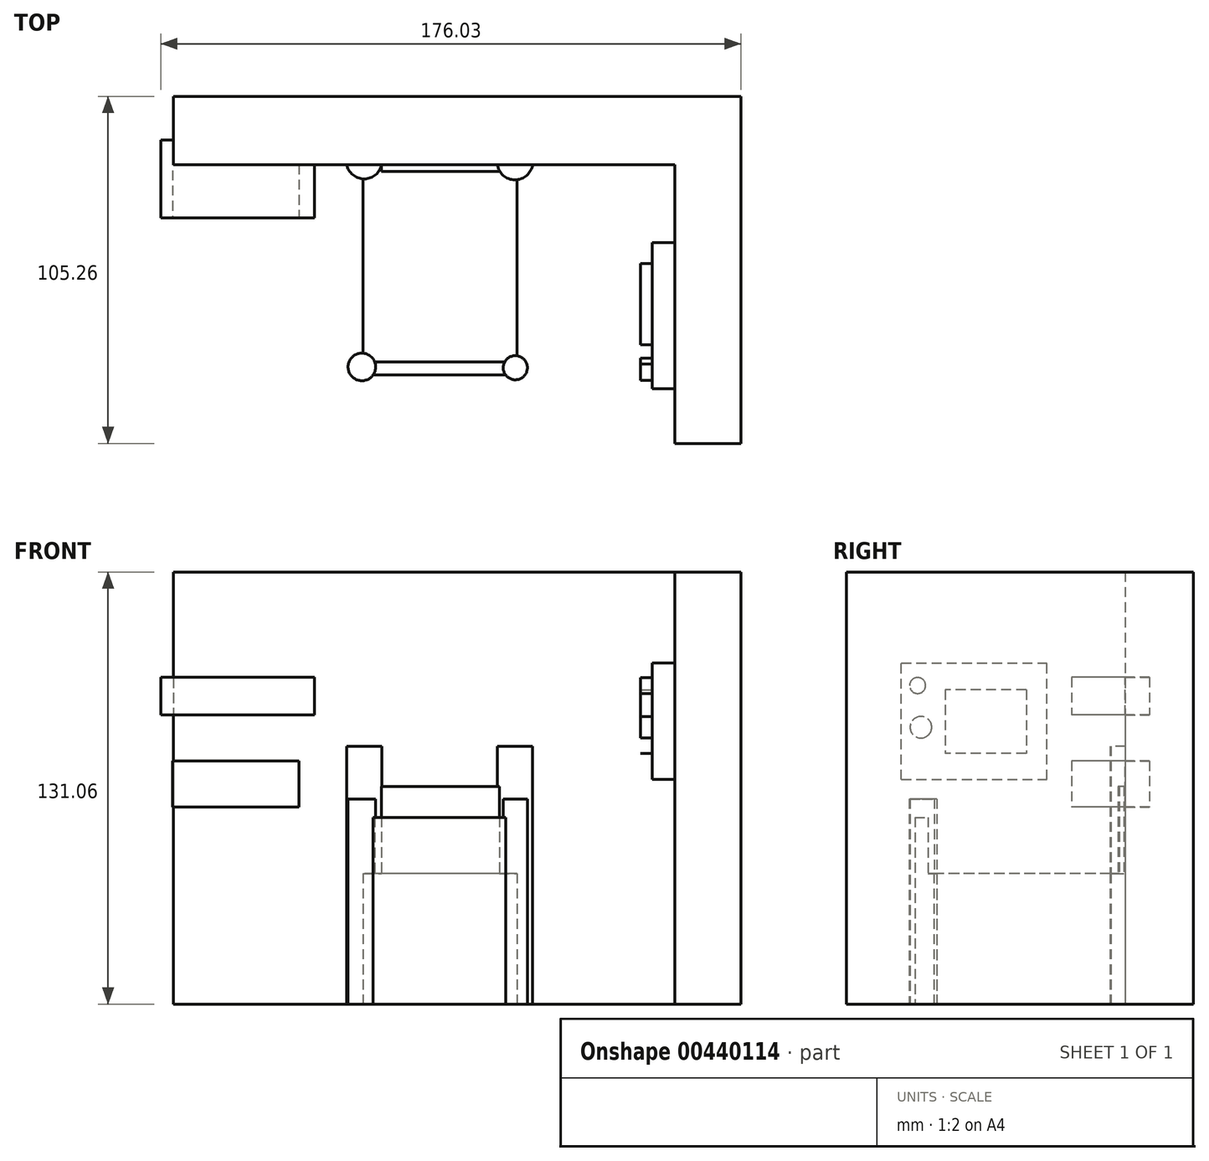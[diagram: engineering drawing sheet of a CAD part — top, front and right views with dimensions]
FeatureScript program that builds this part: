
annotation { "Feature Type Name" : "Feature", "Feature Type Description" : "" }
export const myFeature = defineFeature(function(context is Context, id is Id, definition is map)
    precondition{}
    {
        {
            var Q0;
            Q0=qCreatedBy(makeId("Top.planeOp"),FACE);
            var sketch = newSketch(context, id + "F0", { "sketchPlane" : qUnion([Q0])});
            skLineSegment(sketch, "E0.bottom", {"start": v(-18.65, 8.3) * mm, "end": v(27.98, 8.3) * mm});
            skLineSegment(sketch, "E0.top", {"start": v(-18.65, -53.78) * mm, "end": v(27.98, -53.78) * mm});
            skLineSegment(sketch, "E0.left", {"start": v(-18.65, 8.3) * mm, "end": v(-18.65, -53.78) * mm});
            skLineSegment(sketch, "E0.right", {"start": v(27.98, 8.3) * mm, "end": v(27.98, -53.78) * mm});
            skSolve(sketch);
        }
        {
            var Q0;
            Q0 = qSketchRegion(id + "F0", true);
            extrude(context, id + "F1", {"entities" : qUnion([Q0]), "depth" : 39.62 * mm});
        }
        {
            var Q0;
            Q0=qCreatedBy(makeId("Top.planeOp"),FACE);
            var sketch = newSketch(context, id + "F2", { "sketchPlane" : qUnion([Q0])});
            skCircle(sketch, "E1", {"center": v(-18.36, 8.9) * mm, "radius": 5.42 * mm});
            skCircle(sketch, "E2", {"center": v(27.4, 8.6) * mm, "radius": 5.42 * mm});
            skSolve(sketch);
        }
        {
            var Q0;
            Q0 = qSketchRegion(id + "F2", true);
            extrude(context, id + "F3", {"entities" : qUnion([Q0]), "operationType" : NewBodyOperationType.ADD, "depth" : 78.23 * mm});
        }
        {
            var Q0;
            Q0=qCreatedBy(makeId("Top.planeOp"),FACE);
            var sketch = newSketch(context, id + "F4", { "sketchPlane" : qUnion([Q0])});
            skLineSegment(sketch, "E3.bottom", {"start": v(-13.16, 11.12) * mm, "end": v(22.66, 11.12) * mm});
            skLineSegment(sketch, "E3.top", {"start": v(-13.16, 5.7) * mm, "end": v(22.66, 5.7) * mm});
            skLineSegment(sketch, "E3.left", {"start": v(-13.16, 11.12) * mm, "end": v(-13.16, 5.7) * mm});
            skLineSegment(sketch, "E3.right", {"start": v(22.66, 11.12) * mm, "end": v(22.66, 5.7) * mm});
            skSolve(sketch);
        }
        {
            var Q0;
            Q0 = qSketchRegion(id + "F4", true);
            extrude(context, id + "F5", {"entities" : qUnion([Q0]), "operationType" : NewBodyOperationType.ADD, "depth" : 66.04 * mm});
        }
        {
            var Q0;
            Q0=qCreatedBy(makeId("Top.planeOp"),FACE);
            var sketch = newSketch(context, id + "F6", { "sketchPlane" : qUnion([Q0])});
            skCircle(sketch, "E4", {"center": v(-19.06, -53.57) * mm, "radius": 4.2 * mm});
            skCircle(sketch, "E5", {"center": v(27.5, -53.8) * mm, "radius": 3.66 * mm});
            skSolve(sketch);
        }
        {
            var Q0;
            Q0 = qSketchRegion(id + "F6", true);
            extrude(context, id + "F7", {"entities" : qUnion([Q0]), "operationType" : NewBodyOperationType.ADD, "depth" : 62.23 * mm});
        }
        {
            var Q0;
            Q0=qCreatedBy(makeId("Top.planeOp"),FACE);
            var sketch = newSketch(context, id + "F8", { "sketchPlane" : qUnion([Q0])});
            skLineSegment(sketch, "E6.bottom", {"start": v(-16.51, -52.05) * mm, "end": v(26.53, -52.05) * mm});
            skLineSegment(sketch, "E6.top", {"start": v(-16.51, -55.98) * mm, "end": v(26.53, -55.98) * mm});
            skLineSegment(sketch, "E6.left", {"start": v(-16.51, -52.05) * mm, "end": v(-16.51, -55.98) * mm});
            skLineSegment(sketch, "E6.right", {"start": v(26.53, -52.05) * mm, "end": v(26.53, -55.98) * mm});
            skSolve(sketch);
        }
        {
            var Q0;
            Q0 = qSketchRegion(id + "F8", true);
            extrude(context, id + "F9", {"entities" : qUnion([Q0]), "operationType" : NewBodyOperationType.ADD, "depth" : 56.64 * mm});
        }
        {
            var Q0;
            Q0=qCreatedBy(makeId("Top.planeOp"),FACE);
            var sketch = newSketch(context, id + "F10", { "sketchPlane" : qUnion([Q0])});
            skLineSegment(sketch, "E7.bottom", {"start": v(-76.2, 28.5) * mm, "end": v(75.9, 28.5) * mm});
            skLineSegment(sketch, "E7.top", {"start": v(-76.2, 7.83) * mm, "end": v(75.9, 7.83) * mm});
            skLineSegment(sketch, "E7.left", {"start": v(-76.2, 28.5) * mm, "end": v(-76.2, 7.83) * mm});
            skLineSegment(sketch, "E7.right", {"start": v(75.9, 28.5) * mm, "end": v(75.9, 7.83) * mm});
            skLineSegment(sketch, "E8.bottom", {"start": v(75.9, 28.5) * mm, "end": v(95.98, 28.5) * mm});
            skLineSegment(sketch, "E8.top", {"start": v(75.9, -76.76) * mm, "end": v(95.98, -76.76) * mm});
            skLineSegment(sketch, "E8.left", {"start": v(75.9, 28.5) * mm, "end": v(75.9, -76.76) * mm});
            skLineSegment(sketch, "E8.right", {"start": v(95.98, 28.5) * mm, "end": v(95.98, -76.76) * mm});
            skSolve(sketch);
        }
        {
            var Q0;
            Q0 = qSketchRegion(id + "F10", true);
            extrude(context, id + "F11", {"entities" : qUnion([Q0]), "operationType" : NewBodyOperationType.ADD, "depth" : 131.06 * mm});
        }
        {
            var Q0;
            Q0=qCreatedBy(makeId("Front.planeOp"),FACE);
            var sketch = newSketch(context, id + "F12", { "sketchPlane" : qUnion([Q0])});
            skLineSegment(sketch, "E9.bottom", {"start": v(-80.05, 99.09) * mm, "end": v(-33.4, 99.09) * mm});
            skLineSegment(sketch, "E9.top", {"start": v(-80.05, 87.67) * mm, "end": v(-33.4, 87.67) * mm});
            skLineSegment(sketch, "E9.left", {"start": v(-80.05, 99.09) * mm, "end": v(-80.05, 87.67) * mm});
            skLineSegment(sketch, "E9.right", {"start": v(-33.4, 99.09) * mm, "end": v(-33.4, 87.67) * mm});
            skLineSegment(sketch, "E10.bottom", {"start": v(-76.46, 73.71) * mm, "end": v(-38.2, 73.71) * mm});
            skLineSegment(sketch, "E10.top", {"start": v(-76.46, 59.76) * mm, "end": v(-38.2, 59.76) * mm});
            skLineSegment(sketch, "E10.left", {"start": v(-76.46, 73.71) * mm, "end": v(-76.46, 59.76) * mm});
            skLineSegment(sketch, "E10.right", {"start": v(-38.2, 73.71) * mm, "end": v(-38.2, 59.76) * mm});
            skSolve(sketch);
        }
        {
            var Q0;
            Q0 = qSketchRegion(id + "F12", true);
            extrude(context, id + "F13", {"entities" : qUnion([Q0]), "operationType" : NewBodyOperationType.ADD, "oppositeDirection" : true, "depth" : 15.24 * mm, "hasSecondDirection" : true, "secondDirectionOppositeDirection" : false, "secondDirectionDepth" : 8.38 * mm});
        }
        {
            var Q0;
            Q0=qCreatedBy(makeId("Right.planeOp"),FACE);
            var sketch = newSketch(context, id + "F14", { "sketchPlane" : qUnion([Q0])});
            skLineSegment(sketch, "E11.bottom", {"start": v(-15.92, 103.52) * mm, "end": v(-60.12, 103.52) * mm});
            skLineSegment(sketch, "E11.top", {"start": v(-15.92, 68.09) * mm, "end": v(-60.12, 68.09) * mm});
            skLineSegment(sketch, "E11.left", {"start": v(-15.92, 103.52) * mm, "end": v(-15.92, 68.09) * mm});
            skLineSegment(sketch, "E11.right", {"start": v(-60.12, 103.52) * mm, "end": v(-60.12, 68.09) * mm});
            skSolve(sketch);
        }
        {
            var Q0;
            Q0 = qSketchRegion(id + "F14", true);
            extrude(context, id + "F15", {"entities" : qUnion([Q0]), "operationType" : NewBodyOperationType.ADD, "depth" : 95.76 * mm, "hasSecondDirection" : true, "secondDirectionOppositeDirection" : false, "secondDirectionDepth" : 69.1 * mm});
        }
        {
            var Q0;
            Q0=makeQuery(id+"F11.opExtrude","SWEPT_FACE",FACE,{"disambiguationData":[OSD([sQuery(id+"F10.wireOp",EDGE,"E8.left")])]});
            var sketch = newSketch(context, id + "F16", { "sketchPlane" : qUnion([Q0])});
            skCircle(sketch, "E12", {"center": v(55.16, 96.63) * mm, "radius": 2.42 * mm});
            skCircle(sketch, "E13", {"center": v(54.16, 83.98) * mm, "radius": 3.28 * mm});
            skLineSegment(sketch, "E14.bottom", {"start": v(22.2, 95.3) * mm, "end": v(46.83, 95.3) * mm});
            skLineSegment(sketch, "E14.top", {"start": v(22.2, 75.99) * mm, "end": v(46.83, 75.99) * mm});
            skLineSegment(sketch, "E14.left", {"start": v(22.2, 95.3) * mm, "end": v(22.2, 75.99) * mm});
            skLineSegment(sketch, "E14.right", {"start": v(46.83, 95.3) * mm, "end": v(46.83, 75.99) * mm});
            skSolve(sketch);
        }
        {
            var Q0;
            Q0 = qSketchRegion(id + "F16", true);
            extrude(context, id + "F17", {"entities" : qUnion([Q0]), "operationType" : NewBodyOperationType.ADD, "depth" : 10.4 * mm});
        }
    });
